# Revit family: LOROWERK 19496-000X
name_source: partatom
category: Sanitärinstallationen
revit_build: Autodesk Revit 2017 (Build: 20160225_1515(x64)
units: mm (PartAtom-declared; Revit-internal decimal feet)

## family parameters
Arbeitsebenenbasiert = Nein
Beim Laden mit Abzugskörper schneiden = Nein
Bemaßung runder Anschluss = Durchmesser verwenden
Gemeinsam genutzt = Nein
Immer vertikal = Ja
Raumberechnungspunkt = Nein
Teiletyp = Normal

## types (1)
- LOROWERK 19496-000X
    Anschluss an GLT, GA = Nein
    Beschreibung = LORO-VERSAL Siebeinheit für Umkehrdach, Höhe Siebkorb: 495mm
    Brandschutz mit Klasse R 120 nachrüstbar = Nein
    CONNECTOR0_DIAMETER_dZ_0r = 70 mm
    CONNECTOR0_dZ_00 = 1 mm  [stored 0.00328084 ft]
    CONNECTOR0_ref_dZ = 1 mm  [stored 0.00328084 ft]
    DATANORM = 19496.000X
    Elektrischer Anschluss YesNo = Nein
    GTIN = 4038088092828
    HAN = 19496.000X
    HeinzeBIM = https://www.heinze.de
    Hersteller = LOROWERK K.H. Vahlbrauk GmbH & Co. KG
    Komplettartikel (Einteilig) aus Kombination (Mehrteileausführung) Ablaufgrundkörper und Aufsatzstück = Nein
    Potenzialausgleich (Erdungsanschluss) vorhanden = Nein
    Produktfamilie = LORO-VERSAL Siebeinheit für Umkehrdach, Höhe Siebkorb: 495mm
    Produktklassifikation Text = Zubehoer
    Produktname = LORO-VERSAL Siebeinheit für Umkehrdach, Höhe Siebkorb: 495mm
    Typname = LORO-VERSAL Siebeinheit für Umkehrdach, Höhe Siebkorb: 495mm
    VDIBSN = 1000070000000000000000000000000000000000000000000100000000

note: [stored X ft] marks values corroborated as IEEE doubles in the binary element streams (Revit-internal decimal feet)
